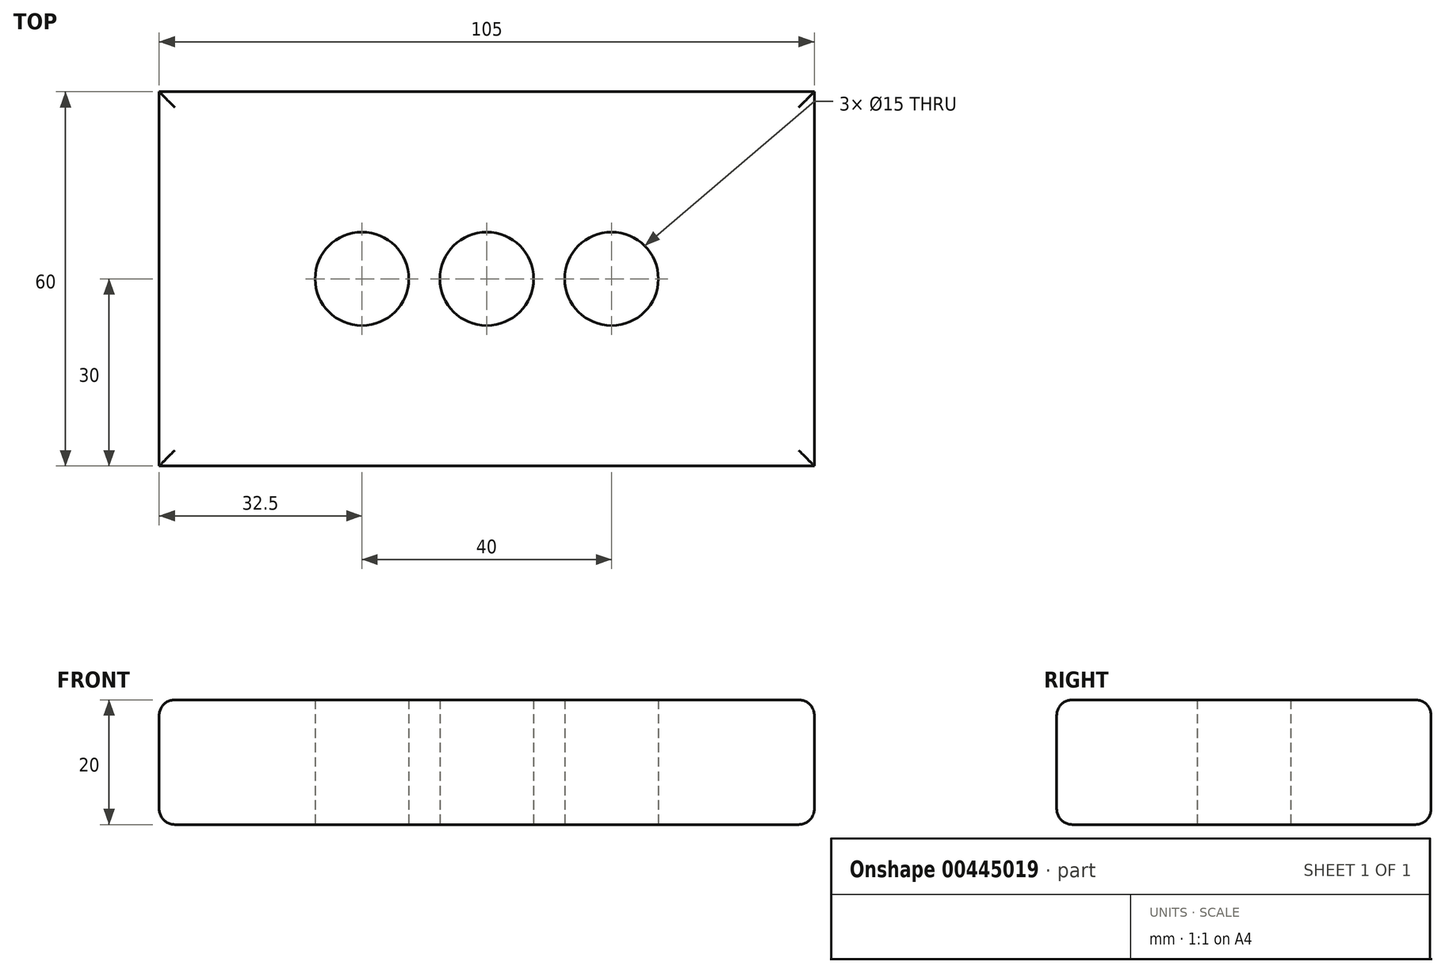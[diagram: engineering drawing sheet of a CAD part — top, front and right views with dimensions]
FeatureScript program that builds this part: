
annotation { "Feature Type Name" : "Feature", "Feature Type Description" : "" }
export const myFeature = defineFeature(function(context is Context, id is Id, definition is map)
    precondition{}
    {
        {
            var Q0;
            Q0=qCreatedBy(makeId("Top.planeOp"),FACE);
            var sketch = newSketch(context, id + "F0", { "sketchPlane" : qUnion([Q0])});
            skLineSegment(sketch, "E0.bottom", {"start": v(52.5, 30) * mm, "end": v(-52.5, 30) * mm});
            skLineSegment(sketch, "E0.top", {"start": v(52.5, -30) * mm, "end": v(-52.5, -30) * mm});
            skLineSegment(sketch, "E0.left", {"start": v(52.5, 30) * mm, "end": v(52.5, -30) * mm});
            skLineSegment(sketch, "E0.right", {"start": v(-52.5, 30) * mm, "end": v(-52.5, -30) * mm});
            skPoint(sketch, "E0.middle", {"position": v(0, 0) * mm});
            skCircle(sketch, "E1", {"center": v(0, 0) * mm, "radius": 7.5 * mm});
            skCircle(sketch, "E2", {"center": v(20, 0) * mm, "radius": 7.5 * mm});
            skCircle(sketch, "E3", {"center": v(-20, 0) * mm, "radius": 7.5 * mm});
            skSolve(sketch);
        }
        {
            var Q0;
            Q0=makeQuery(id+"F0.imprint","IMPRINT",FACE,{"disambiguationData":[TD([[makeQuery(id+"F0.imprint","IMPRINT",EDGE,{"derivedFrom":sQuery(id+"F0.wireOp",EDGE,"E0.bottom")}),1.0]])]});
            extrude(context, id + "F1", {"entities" : qUnion([Q0]), "depth" : 20 * mm});
        }
        {
            var Q0;
            Q0=makeQuery(id+"F1.opExtrude","CAP_EDGE",EDGE,{"disambiguationData":[OSD([sQuery(id+"F0.wireOp",EDGE,"E0.right")])],"isStart":false});
            var Q1;
            Q1=makeQuery(id+"F1.opExtrude","CAP_EDGE",EDGE,{"disambiguationData":[OSD([sQuery(id+"F0.wireOp",EDGE,"E0.top")])],"isStart":false});
            var Q2;
            Q2=makeQuery(id+"F1.opExtrude","CAP_EDGE",EDGE,{"disambiguationData":[OSD([sQuery(id+"F0.wireOp",EDGE,"E0.left")])],"isStart":false});
            var Q3;
            Q3=makeQuery(id+"F1.opExtrude","CAP_EDGE",EDGE,{"disambiguationData":[OSD([sQuery(id+"F0.wireOp",EDGE,"E0.bottom")])],"isStart":false});
            var Q4;
            Q4=makeQuery(id+"F1.opExtrude","CAP_EDGE",EDGE,{"disambiguationData":[OSD([sQuery(id+"F0.wireOp",EDGE,"E0.left")])],"isStart":true});
            var Q5;
            Q5=makeQuery(id+"F1.opExtrude","CAP_EDGE",EDGE,{"disambiguationData":[OSD([sQuery(id+"F0.wireOp",EDGE,"E0.top")])],"isStart":true});
            var Q6;
            Q6=makeQuery(id+"F1.opExtrude","CAP_EDGE",EDGE,{"disambiguationData":[OSD([sQuery(id+"F0.wireOp",EDGE,"E0.right")])],"isStart":true});
            var Q7;
            Q7=makeQuery(id+"F1.opExtrude","CAP_EDGE",EDGE,{"disambiguationData":[OSD([sQuery(id+"F0.wireOp",EDGE,"E0.bottom")])],"isStart":true});
            fillet(context, id + "F2", {"entities" : qUnion([Q0, Q1, Q2, Q3, Q4, Q5, Q6, Q7]), "radius" : 2.5 * mm, "tangentPropagation" : true, "allowEdgeOverflow" : false});
        }
    });
